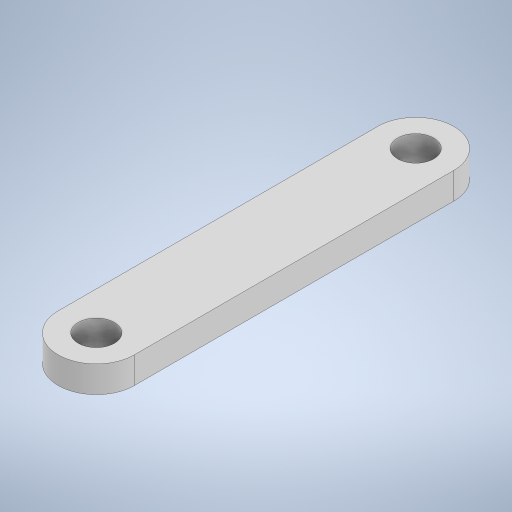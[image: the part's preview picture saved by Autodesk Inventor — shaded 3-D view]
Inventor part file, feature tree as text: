
AUTODESK INVENTOR PART (.ipt)
format: ipt  version: 2024 (Build 280153000, 153)  size: 228,352 bytes
history: native  units: in
note: dims shown in document units (in); Inventor stores cm internally (conversion verified against a paired STEP export)
features: extrude x1, sketch x1
ambient origin geometry x8: Origin, YZ Plane, XZ Plane, XY Plane, X Axis, Y Axis, Z Axis, Center Point
bodies: Solid1 (feature_tree)
feature tree (2):
  extrude  "Extrusion1"  Depth=0.125in
  sketch  "Sketch1"  dims[d0=0.17in d1=0.17in d2=1.5in d3=0.0938in d4=0.0938in d5=0.125in d6=0.0in]
